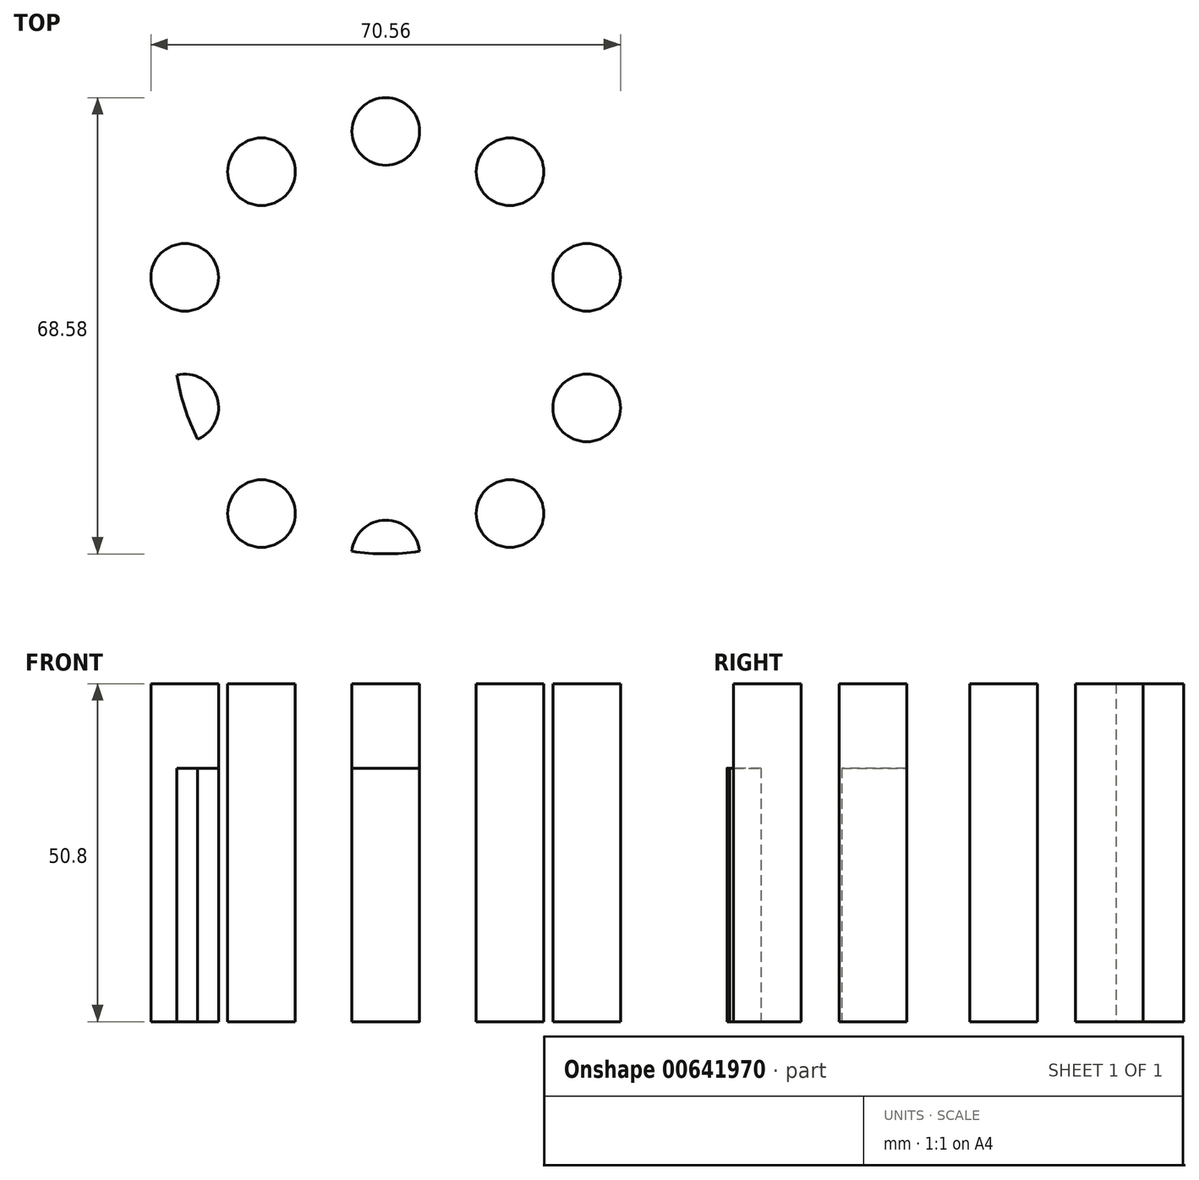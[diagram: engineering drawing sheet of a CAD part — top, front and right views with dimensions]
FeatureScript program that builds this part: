
annotation { "Feature Type Name" : "Feature", "Feature Type Description" : "" }
export const myFeature = defineFeature(function(context is Context, id is Id, definition is map)
    precondition{}
    {
        {
            var Q0;
            Q0=qCreatedBy(makeId("Top.planeOp"),FACE);
            var sketch = newSketch(context, id + "F0", { "sketchPlane" : qUnion([Q0])});
            skCircle(sketch, "E0", {"center": v(0, 0) * mm, "radius": 31.75 * mm});
            skSolve(sketch);
        }
        {
            var Q0;
            Q0=qSketchRegion(id+"F0",true);
            extrude(context, id + "F1", {"entities" : qUnion([Q0]), "depth" : 38.1 * mm});
        }
        {
            var Q0;
            Q0=qCreatedBy(makeId("Top.planeOp"),FACE);
            var sketch = newSketch(context, id + "F2", { "sketchPlane" : qUnion([Q0])});
            skCircle(sketch, "E1", {"center": v(0, 31.75) * mm, "radius": 5.08 * mm});
            skCircle(sketch, "E2.1.0", {"center": v(-18.66, 25.69) * mm, "radius": 5.08 * mm});
            skCircle(sketch, "E2.2.0", {"center": v(-30.2, 9.81) * mm, "radius": 5.08 * mm});
            skCircle(sketch, "E2.3.0", {"center": v(-30.2, -9.81) * mm, "radius": 5.08 * mm});
            skCircle(sketch, "E2.4.0", {"center": v(-18.66, -25.69) * mm, "radius": 5.08 * mm});
            skCircle(sketch, "E2.5.0", {"center": v(0, -31.75) * mm, "radius": 5.08 * mm});
            skCircle(sketch, "E2.6.0", {"center": v(18.66, -25.69) * mm, "radius": 5.08 * mm});
            skCircle(sketch, "E2.7.0", {"center": v(30.2, -9.81) * mm, "radius": 5.08 * mm});
            skCircle(sketch, "E2.8.0", {"center": v(30.2, 9.81) * mm, "radius": 5.08 * mm});
            skCircle(sketch, "E2.9.0", {"center": v(18.66, 25.69) * mm, "radius": 5.08 * mm});
            skPoint(sketch, "E2.center", {"position": v(0, 0) * mm});
            skSolve(sketch);
        }
        {
            var Q0;
            Q0=qSketchRegion(id+"F2",true);
            extrude(context, id + "F3", {"entities" : qUnion([Q0]), "depth" : 50.8 * mm});
        }
        {
            var Q0;
            Q0=makeQuery(id+"F1.opExtrude","SWEPT_BODY",BODY,{"disambiguationData":[OSD([sQuery(id+"F0.wireOp",EDGE,"E0")])]});
            var Q1;
            Q1=makeQuery(id+"F3.opExtrude","SWEPT_BODY",BODY,{"disambiguationData":[OSD([sQuery(id+"F2.wireOp",EDGE,"E1")])]});
            var Q2;
            Q2=makeQuery(id+"F3.opExtrude","SWEPT_BODY",BODY,{"disambiguationData":[OSD([sQuery(id+"F2.wireOp",EDGE,"E2.1.0")])]});
            var Q3;
            Q3=makeQuery(id+"F3.opExtrude","SWEPT_BODY",BODY,{"disambiguationData":[OSD([sQuery(id+"F2.wireOp",EDGE,"E2.2.0")])]});
            var Q4;
            Q4=makeQuery(id+"F3.opExtrude","SWEPT_BODY",BODY,{"disambiguationData":[OSD([sQuery(id+"F2.wireOp",EDGE,"E2.3.0")])]});
            var Q5;
            Q5=makeQuery(id+"F3.opExtrude","SWEPT_BODY",BODY,{"disambiguationData":[OSD([sQuery(id+"F2.wireOp",EDGE,"E2.4.0")])]});
            var Q6;
            Q6=makeQuery(id+"F3.opExtrude","SWEPT_BODY",BODY,{"disambiguationData":[OSD([sQuery(id+"F2.wireOp",EDGE,"E2.5.0")])]});
            var Q7;
            Q7=makeQuery(id+"F3.opExtrude","SWEPT_BODY",BODY,{"disambiguationData":[OSD([sQuery(id+"F2.wireOp",EDGE,"E2.6.0")])]});
            var Q8;
            Q8=makeQuery(id+"F3.opExtrude","SWEPT_BODY",BODY,{"disambiguationData":[OSD([sQuery(id+"F2.wireOp",EDGE,"E2.7.0")])]});
            var Q9;
            Q9=makeQuery(id+"F3.opExtrude","SWEPT_BODY",BODY,{"disambiguationData":[OSD([sQuery(id+"F2.wireOp",EDGE,"E2.8.0")])]});
            var Q10;
            Q10=makeQuery(id+"F3.opExtrude","SWEPT_BODY",BODY,{"disambiguationData":[OSD([sQuery(id+"F2.wireOp",EDGE,"E2.9.0")])]});
            booleanBodies(context, id + "F4", {"operationType" : BooleanOperationType.INTERSECTION, "tools" : qUnion([Q0, Q1, Q2, Q3, Q4, Q5, Q6, Q7, Q8, Q9, Q10]), "keepTools" : true});
        }
        {
            var Q0;
            Q0=makeQuery(id+"F3.opExtrude","SWEPT_BODY",BODY,{"disambiguationData":[OSD([sQuery(id+"F2.wireOp",EDGE,"E2.3.0")])]});
            var Q1;
            Q1=makeQuery(id+"F1.opExtrude","SWEPT_BODY",BODY,{"disambiguationData":[OSD([sQuery(id+"F0.wireOp",EDGE,"E0")])]});
            booleanBodies(context, id + "F5", {"operationType" : BooleanOperationType.INTERSECTION, "tools" : qUnion([Q0, Q1]), "keepTools" : true});
        }
        {
            var Q0;
            Q0=makeQuery(id+"F1.opExtrude","SWEPT_BODY",BODY,{"disambiguationData":[OSD([sQuery(id+"F0.wireOp",EDGE,"E0")])]});
            var Q1;
            Q1=makeQuery(id+"F3.opExtrude","SWEPT_BODY",BODY,{"disambiguationData":[OSD([sQuery(id+"F2.wireOp",EDGE,"E2.5.0")])]});
            booleanBodies(context, id + "F6", {"operationType" : BooleanOperationType.INTERSECTION, "tools" : qUnion([Q0, Q1]), "keepTools" : true});
        }
        {
            var Q0;
            Q0=makeQuery(id+"F3.opExtrude","SWEPT_BODY",BODY,{"disambiguationData":[OSD([sQuery(id+"F2.wireOp",EDGE,"E2.5.0")])]});
            var Q1;
            Q1=makeQuery(id+"F3.opExtrude","SWEPT_BODY",BODY,{"disambiguationData":[OSD([sQuery(id+"F2.wireOp",EDGE,"E2.3.0")])]});
            var Q2;
            Q2=makeQuery(id+"F1.opExtrude","SWEPT_BODY",BODY,{"disambiguationData":[OSD([sQuery(id+"F0.wireOp",EDGE,"E0")])]});
            deleteBodies(context, id + "F7", {"entities" : qUnion([Q0, Q1, Q2])});
        }
    });
